# Revit family: Haworth_Epure_SideBench_FixedLegs_AP_PRELIMINARY
name_source: partatom
category: Furniture
units: mm (PartAtom-declared; Revit-internal decimal feet)

## family parameters
Always vertical = Yes
Cut with Voids When Loaded = No
OmniClass Number = 23.40.70.14.64.11
OmniClass Title = Office Furniture
Room Calculation Point = No
Shared = No
Work Plane-Based = No

## types (6) — shared parameters
Actual Height = 730 mm  [stored 2.39501 ft]
Assembly Code = E2020200
Cable Tray Finish = Haworth _ Polymer _ Undecided
Description = Haworth - Epure - Side Bench - Fixed Legs
Flip Top Finish = Haworth _ Paint _ Metallic Silver
Leg Height = 695 mm  [stored 2.28018 ft]
Manufacturer = Haworth
Model = SYEPSDFXXXX
Revision Number = 1
Size = Verify Final Dim.w/ Haworth
Trim Finish = Haworth _ Metal _ Structured White EC
URL = https://www.haworth.com
URL - Product = https://www.haworth.com
Warranty = http://www.haworth.com
Wooden C = No
Wooden L2 = No
Worksurface Depth = 1200, 1400, 1500, 1600 mm
Worksurface Width = 600, 700, 750, 800 mm

## per-type parameters (varying)
| type | Accessory Kit | Actual Depth | Actual Width | Aluminium C | Aluminium L1 | Aluminium L2 | Aluminium Legs | Aluminium R1 | Cable Tray | Cable Tray Width | End Frame | Flip Top Cable Outlet | No Accessory Kit | Start Frame | Umbilical Cord | Wooden L1 | Wooden Legs | Wooden R1 |
| 800 x 1600 | Yes | 1600 mm  [stored 5.24934 ft] | 800 mm  [stored 2.62467 ft] | No | No | No | No | No | Yes | 800 mm  [stored 2.62467 ft] | Yes | Yes | No | No | Yes | Yes | Yes | Yes |
| 600 x 1200 | No | 1200 mm | 600 mm | Yes | Yes | Yes | Yes | Yes | No | 400 mm | No | No | Yes | Yes | No | No | No | No |
| 700 x 1500 | Yes | 1500 mm  [stored 4.92126 ft] | 700 mm | No | No | No | No | No | Yes | 700 mm | Yes | No | No | No | No | Yes | Yes | Yes |
| 750 x 1400 | Yes | 1400 mm | 750 mm  [stored 2.46063 ft] | Yes | Yes | Yes | Yes | Yes | Yes | 600 mm | No | Yes | No | Yes | No | No | No | No |
| 750 x 1600 | Yes | 1600 mm  [stored 5.24934 ft] | 750 mm  [stored 2.46063 ft] | No | No | No | No | No | Yes | 800 mm  [stored 2.62467 ft] | Yes | Yes | No | No | Yes | Yes | Yes | Yes |
| 800 x 1400 | No | 1400 mm | 800 mm  [stored 2.62467 ft] | Yes | Yes | Yes | Yes | Yes | No | 600 mm | No | No | Yes | Yes | No | No | No | No |

note: [stored X ft] marks values corroborated as IEEE doubles in the binary element streams (Revit-internal decimal feet)

## geometry (parser evidence)
native form markers: Sweep x32
no freeform markers — native parametric forms only
